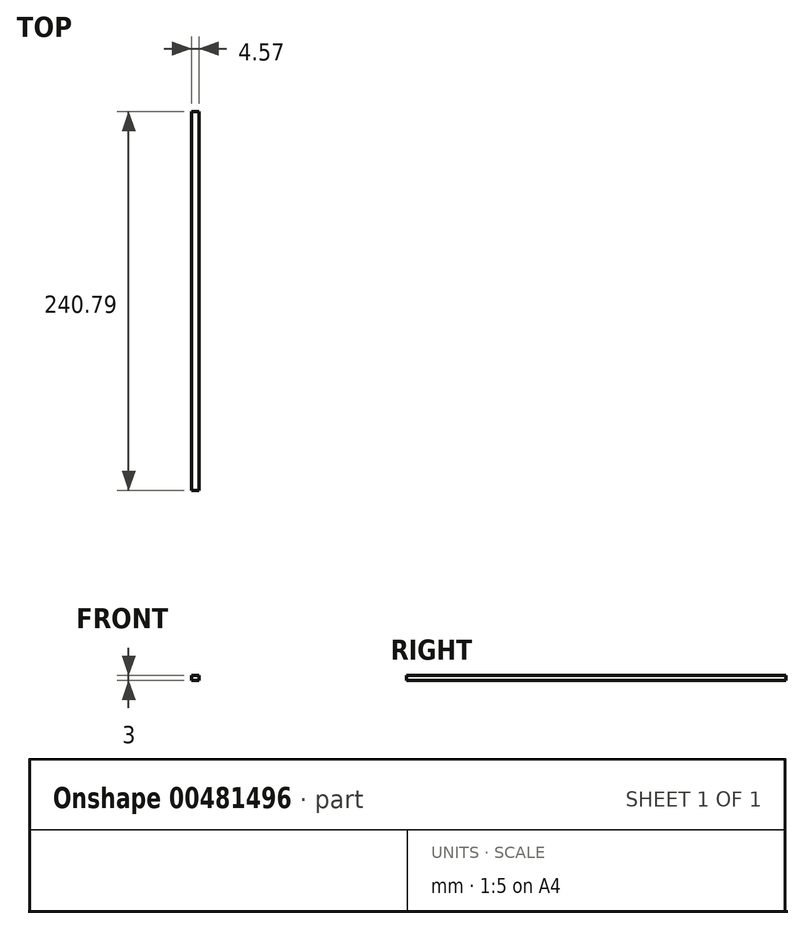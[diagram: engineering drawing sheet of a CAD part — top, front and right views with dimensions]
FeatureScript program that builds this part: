
annotation { "Feature Type Name" : "Feature", "Feature Type Description" : "" }
export const myFeature = defineFeature(function(context is Context, id is Id, definition is map)
    precondition{}
    {
        {
            var Q0;
            Q0=qCreatedBy(makeId("Top.planeOp"),FACE);
            var sketch = newSketch(context, id + "F0", { "sketchPlane" : qUnion([Q0])});
            skLineSegment(sketch, "E0.bottom", {"start": v(-1.98, 101.9) * mm, "end": v(-6.55, 101.9) * mm});
            skLineSegment(sketch, "E0.top", {"start": v(-1.98, -138.89) * mm, "end": v(-6.55, -138.89) * mm});
            skLineSegment(sketch, "E0.left", {"start": v(-1.98, 101.9) * mm, "end": v(-1.98, -138.89) * mm});
            skLineSegment(sketch, "E0.right", {"start": v(-6.55, 101.9) * mm, "end": v(-6.55, -138.89) * mm});
            skSolve(sketch);
        }
        {
            var Q0;
            Q0 = qSketchRegion(id + "F0", true);
            extrude(context, id + "F1", {"entities" : qUnion([Q0]), "depth" : 3 * mm});
        }
    });
